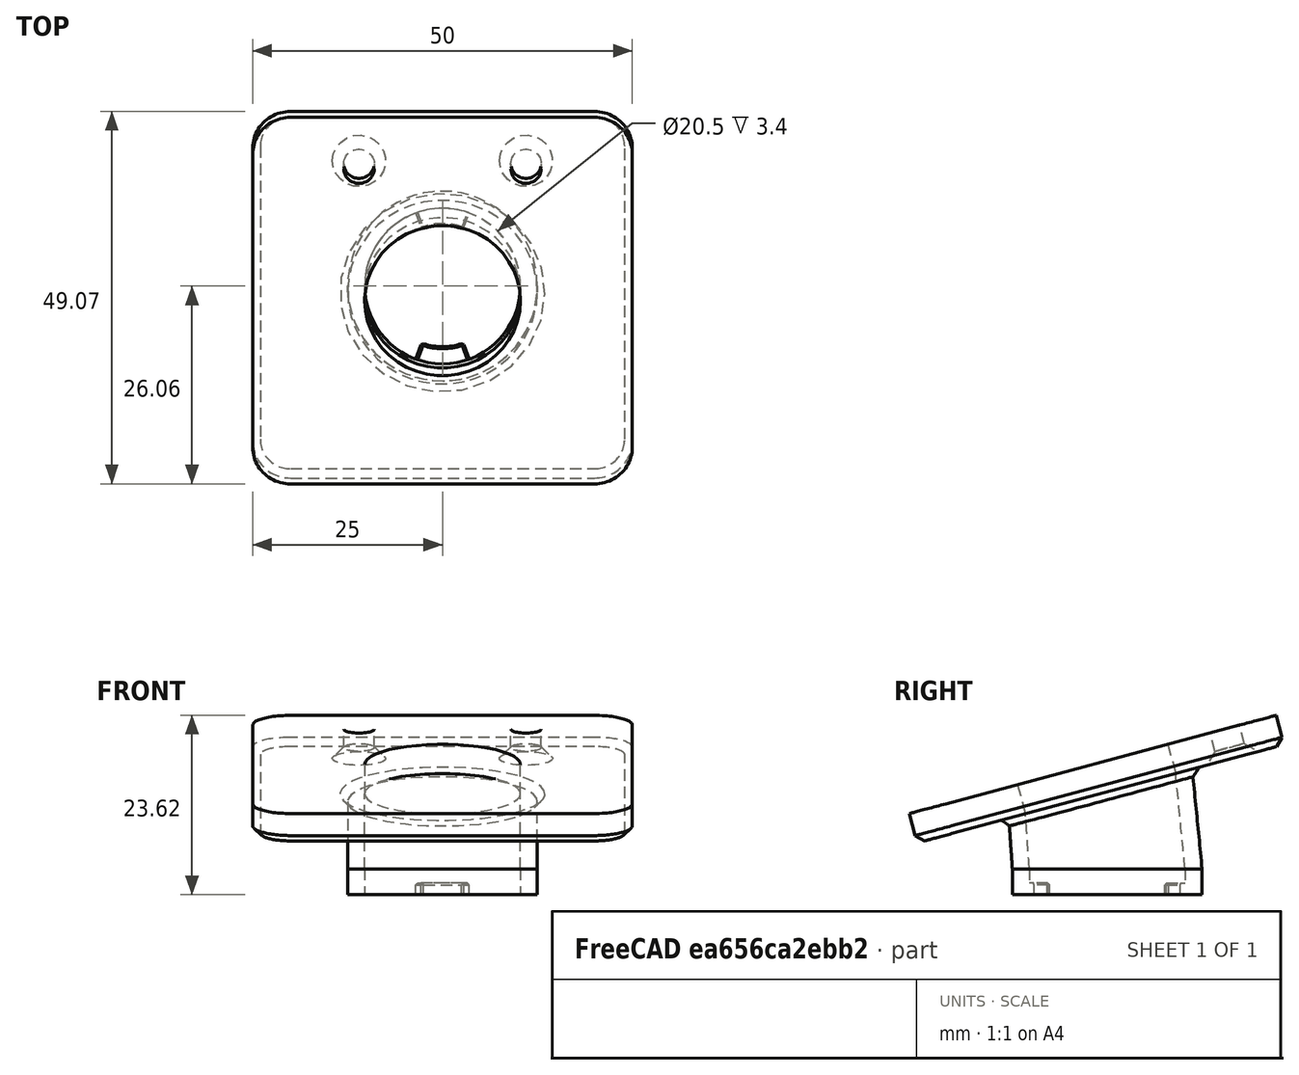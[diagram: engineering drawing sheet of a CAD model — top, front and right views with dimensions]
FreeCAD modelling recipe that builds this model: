
FCSTD DOCUMENT  (FreeCAD 1.1R44874 (Git))
Label: solar_sensor_mount
License: All rights reserved
LicenseURL: https://en.wikipedia.org/wiki/All_rights_reserved
objects: Sketcher::SketchObject×5, PartDesign::Pad×3, PartDesign::PolarPattern×2, PartDesign::Chamfer×2, App::Point×1, PartDesign::SubShapeBinder×1, PartDesign::AdditiveLoft×1, PartDesign::Fillet×1, PartDesign::Hole×1, Part::DatumPlane×1, PartDesign::Body×1
note: 40 computed .brp shape members not serialized (recipe doc carries the construction recipe); baked Part::Feature solids carry a one-line shape summary decoded from their .brp

FEATURE [App::Point] Origin001
  Role = Origin
FEATURE [Sketcher::SketchObject] Sketch
  ArcFitTolerance = 1e-06
  AttachmentSupport = -> [Origin]
  ExternalTypes = [0]
  FullyConstrained = true
  MakeInternals = false
  MapMode = 5
  _ExternalGeoVersion = 1
  sketch-geometry (2):
    g0: Circle CenterX=0 CenterY=0 CenterZ=0 NormalX=0 NormalY=0 NormalZ=1 AngleXU=0 Radius=12.5
    g1: Circle CenterX=0 CenterY=0 CenterZ=0 NormalX=0 NormalY=0 NormalZ=1 AngleXU=0 Radius=10.25
  constraints (4):
    c: Coincident(g1,g0)
    c: Diameter(g0) = 25
    c: Diameter(g1) = 20.5
    c: Coincident(g0,g-1)
FEATURE [PartDesign::Pad] Pad
  Direction = (0,0,1)
  Length = 3.4
  Length2 = 10
  Profile = -> Sketch
  ReferenceAxis = -> Sketch [N_Axis]
  Refine = true
  SideType = 0
  Suppressed = false
  Type = 0
  Type2 = 0
FEATURE [Sketcher::SketchObject] Sketch001
  ArcFitTolerance = 1e-06
  AttachmentSupport = -> [Origin]
  ExternalGeometry = -> [Pad]
  ExternalTypes = [0]
  FullyConstrained = true
  MakeInternals = false
  MapMode = 5
  _ExternalGeoVersion = 1
  sketch-geometry (7):
    g0: ArcOfCircle CenterX=0 CenterY=0 CenterZ=0 NormalX=0 NormalY=0 NormalZ=1 AngleXU=0 Radius=8 StartAngle=1.21989 EndAngle=1.9217
    g1: ArcOfCircle CenterX=0 CenterY=0 CenterZ=0 NormalX=0 NormalY=0 NormalZ=1 AngleXU=0 Radius=10.25 StartAngle=1.21989 EndAngle=1.9217
    g2: LineSegment StartX=-3.52344 StartY=9.62538 StartZ=0 EndX=-2.75 EndY=7.51249 EndZ=0
    g3: LineSegment [constr] StartX=-2.75 StartY=7.51249 StartZ=0 EndX=0 EndY=0 EndZ=0
    g4: LineSegment [constr] StartX=0 StartY=0 StartZ=0 EndX=2.75 EndY=7.51249 EndZ=0
    g5: LineSegment StartX=2.75 StartY=7.51249 StartZ=0 EndX=3.52344 EndY=9.62538 EndZ=0
    g6: LineSegment [constr] StartX=-2.75 StartY=7.51249 StartZ=0 EndX=2.75 EndY=7.51249 EndZ=0
  constraints (19):
    c: Coincident(g0,g-1)
    c: Coincident(g1,g0)
    c: PointOnObject(g1,g-3)
    c: Coincident(g1,g2)
    c: Coincident(g2,g3)
    c: Coincident(g3,g0)
    c: Coincident(g3,g4)
    c: Coincident(g4,g0)
    c: Coincident(g4,g5)
    c: Coincident(g5,g1)
    c: Parallel(g2,g3)
    c: Parallel(g5,g4)
    c: Diameter(g0) = 16
    c: Coincident(g2,g0)
    c: Symmetric(g0,g0,g-2)
    c: PointOnObject(g6,g3)
    c: Coincident(g6,g0)
    c: Horizontal(g6)
    c: DistanceX(g6,g6) = 5.5
FEATURE [PartDesign::Pad] Pad001
  BaseFeature = -> Pad
  Direction = (0,0,1)
  Length = 1.5
  Length2 = 10
  Profile = -> Sketch001
  ReferenceAxis = -> Sketch001 [N_Axis]
  Refine = true
  SideType = 0
  Suppressed = false
  Type = 0
  Type2 = 0
FEATURE [PartDesign::PolarPattern] PolarPattern
  Angle = 360
  Axis = -> Z_Axis
  BaseFeature = -> Pad001
  Mode = 0
  Occurrences = 2
  Offset = 120
  Originals = -> [Pad001]
  Refine = true
  SpacingPattern = [0]
  Spacings = [-1]
  Suppressed = false
  TransformMode = 0
FEATURE [PartDesign::Chamfer] Chamfer
  Angle = 45
  Base = -> PolarPattern [Edge22,Edge20,Edge17,Edge15,Edge18]
  BaseFeature = -> PolarPattern
  ChamferType = 0
  FlipDirection = false
  Refine = true
  Size = 0.25
  Size2 = 1
  SupportTransform = false
  Suppressed = false
  UseAllEdges = false
FEATURE [PartDesign::PolarPattern] PolarPattern001
  Angle = 360
  Axis = -> Z_Axis
  BaseFeature = -> Chamfer
  Mode = 0
  Occurrences = 2
  Offset = 120
  Originals = -> [Chamfer]
  Refine = true
  SpacingPattern = [0]
  Spacings = [-1]
  Suppressed = false
  TransformMode = 0
FEATURE [PartDesign::SubShapeBinder] Binder
  BindCopyOnChange = 0
  BindMode = 0
  ClaimChildren = false
  Context = -> Body [Binder.]
  Fuse = false
  MakeFace = true
  OffsetFill = false
  OffsetIntersection = false
  OffsetJoinType = 0
  OffsetOpenResult = false
  PartialLoad = false
  Placement = pos=(0,0,10) rot=(1,0,0;0.261799rad)
  Refine = true
  Relative = true
  Support = -> [PolarPattern001[Face16]]
  _Version = 2
FEATURE [Sketcher::SketchObject] Sketch002
  ArcFitTolerance = 1e-06
  AttachmentSupport = -> [Binder]
  ExternalGeometry = -> [Binder]
  ExternalTypes = [0]
  FullyConstrained = true
  MakeInternals = false
  MapMode = 5
  Placement = pos=(0,-0.879985,13.2841) rot=(1,0,0;0.261799rad)
  _ExternalGeoVersion = 1
  sketch-geometry (7):
    g0: LineSegment StartX=-25 StartY=-25 StartZ=0 EndX=25 EndY=-25 EndZ=0
    g1: LineSegment StartX=25 StartY=-25 StartZ=0 EndX=25 EndY=25 EndZ=0
    g2: LineSegment StartX=25 StartY=25 StartZ=0 EndX=-25 EndY=25 EndZ=0
    g3: LineSegment StartX=-25 StartY=25 StartZ=0 EndX=-25 EndY=-25 EndZ=0
    g4: GeomPoint [constr] X=0 Y=0 Z=0
    g5: Circle [constr] CenterX=-11 CenterY=20 CenterZ=0 NormalX=0 NormalY=0 NormalZ=1 AngleXU=0 Radius=2
    g6: Circle [constr] CenterX=11 CenterY=20 CenterZ=0 NormalX=0 NormalY=0 NormalZ=1 AngleXU=0 Radius=2
  constraints (17):
    c: Coincident(g0,g1)
    c: Coincident(g1,g2)
    c: Coincident(g2,g3)
    c: Coincident(g3,g0)
    c: Horizontal(g0)
    c: Horizontal(g2)
    c: Vertical(g1)
    c: Vertical(g3)
    c: Symmetric(g2,g0,g4)
    c: Coincident(g4,g-1)
    c: Equal(g2,g1)
    c: Symmetric(g5,g6,g-2)
    c: Equal(g5,g6)
    c: Diameter(g5) = 4
    c: DistanceX(g5,g6) = 22
    c: DistanceY(g4,g5) = 20
    c: DistanceY(g5,g2) = 5
FEATURE [PartDesign::AdditiveLoft] AdditiveLoft
  BaseFeature = -> PolarPattern001
  Closed = false
  Profile = -> PolarPattern001 [Face16]
  Refine = true
  Ruled = false
  Sections = -> [Binder]
  Suppressed = false
FEATURE [PartDesign::Pad] Pad002
  BaseFeature = -> AdditiveLoft
  Direction = (0,-0.258819,0.965926)
  Length = 4
  Length2 = 10
  Profile = -> Sketch002
  ReferenceAxis = -> Sketch002 [N_Axis]
  Refine = true
  SideType = 0
  Suppressed = false
  Type = 0
  Type2 = 0
FEATURE [PartDesign::Fillet] Fillet
  Base = -> Pad002 [Edge78,Edge75,Edge77,Edge76]
  BaseFeature = -> Pad002
  Radius = 5
  Refine = true
  SupportTransform = false
  Suppressed = false
  UseAllEdges = false
FEATURE [PartDesign::Chamfer] Chamfer001
  Angle = 45
  Base = -> Fillet [Face11]
  BaseFeature = -> Fillet
  ChamferType = 0
  FlipDirection = false
  Refine = true
  Size = 1
  Size2 = 1
  SupportTransform = false
  Suppressed = false
  UseAllEdges = false
FEATURE [Sketcher::SketchObject] Sketch003
  ArcFitTolerance = 1e-06
  AttachmentSupport = -> [Binder]
  ExternalTypes = [0]
  FullyConstrained = true
  MakeInternals = false
  MapMode = 5
  Placement = pos=(0,-0.879985,13.2841) rot=(1,0,0;0.261799rad)
  _ExternalGeoVersion = 1
  sketch-geometry (2):
    g0: Circle CenterX=-11 CenterY=18 CenterZ=0 NormalX=0 NormalY=0 NormalZ=1 AngleXU=0 Radius=1.5
    g1: Circle CenterX=11 CenterY=18 CenterZ=0 NormalX=0 NormalY=0 NormalZ=1 AngleXU=0 Radius=1.5
  constraints (5):
    c: Symmetric(g0,g1,g-2)
    c: Equal(g0,g1)
    c: DistanceY(g-1,g0) = 18
    c: DistanceX(g0,g1) = 22
    c: Diameter(g0) = 3
FEATURE [PartDesign::Hole] Hole
  BaseFeature = -> Chamfer001
  BaseProfileType = 7
  CustomThreadClearance = 0
  Depth = 25
  DepthType = 0
  Diameter = 4
  DrillForDepth = false
  DrillPoint = 1
  DrillPointAngle = 118
  HoleCutCountersinkAngle = 90
  HoleCutCustomValues = false
  HoleCutDepth = 3.5
  HoleCutDiameter = 7
  HoleCutType = 2
  ModelThread = false
  Profile = -> Sketch003
  Refine = true
  Reversed = true
  Suppressed = false
  Tapered = false
  TaperedAngle = 90
  ThreadClass = 0
  ThreadDepth = 25
  ThreadDepthType = 0
  ThreadDiameter = 4
  ThreadDirection = 0
  ThreadFit = 0
  ThreadSize = 0
  ThreadType = 0
  Threaded = false
  UseCustomThreadClearance = false
FEATURE [Part::DatumPlane] DatumPlane
  AttachmentSupport = -> [Pad001]
  MapMode = 5
  Placement = pos=(0,0,3.4) rot=(0,0,1;0rad)
FEATURE [Sketcher::SketchObject] Sketch004
  ArcFitTolerance = 1e-06
  AttachmentSupport = -> [DatumPlane]
  ExternalTypes = [0]
  FullyConstrained = true
  MakeInternals = false
  MapMode = 5
  Placement = pos=(0,0,3.4) rot=(0,0,1;0rad)
  _ExternalGeoVersion = 1
  sketch-geometry (13):
    g0: LineSegment StartX=-25 StartY=-35 StartZ=0 EndX=25 EndY=-35 EndZ=0
    g1: LineSegment StartX=35 StartY=-25 StartZ=0 EndX=35 EndY=25 EndZ=0
    g2: LineSegment StartX=25 StartY=35 StartZ=0 EndX=-25 EndY=35 EndZ=0
    g3: LineSegment StartX=-35 StartY=25 StartZ=0 EndX=-35 EndY=-25 EndZ=0
    g4: GeomPoint [constr] X=0 Y=0 Z=0
    g5: ArcOfCircle CenterX=25 CenterY=25 CenterZ=0 NormalX=0 NormalY=0 NormalZ=1 AngleXU=0 Radius=10 StartAngle=0 EndAngle=1.5708
    g6: GeomPoint [constr] X=35 Y=35 Z=0
    g7: ArcOfCircle CenterX=25 CenterY=-25 CenterZ=0 NormalX=0 NormalY=0 NormalZ=1 AngleXU=0 Radius=10 StartAngle=4.71239 EndAngle=6.28319
    g8: GeomPoint [constr] X=35 Y=-35 Z=0
    g9: ArcOfCircle CenterX=-25 CenterY=-25 CenterZ=0 NormalX=0 NormalY=0 NormalZ=1 AngleXU=0 Radius=10 StartAngle=3.14159 EndAngle=4.71239
    g10: GeomPoint [constr] X=-35 Y=-35 Z=0
    g11: ArcOfCircle CenterX=-25 CenterY=25 CenterZ=0 NormalX=0 NormalY=0 NormalZ=1 AngleXU=0 Radius=10 StartAngle=1.5708 EndAngle=3.14159
    g12: GeomPoint [constr] X=-35 Y=35 Z=0
  constraints (28):
    c: Horizontal(g0)
    c: Horizontal(g2)
    c: Vertical(g1)
    c: Vertical(g3)
    c: Symmetric(g6,g10,g4)
    c: Distance(g8,g10) = 70
    c: PointOnObject(g6,g2)
    c: PointOnObject(g6,g1)
    c: Tangent(g2,g5) = -1.5708
    c: Tangent(g1,g5) = -1.5708
    c: PointOnObject(g8,g0)
    c: PointOnObject(g8,g1)
    c: Tangent(g0,g7) = -1.5708
    c: Tangent(g1,g7) = -1.5708
    c: PointOnObject(g10,g0)
    c: PointOnObject(g10,g3)
    c: Tangent(g0,g9) = -1.5708
    c: Tangent(g3,g9) = -1.5708
    c: PointOnObject(g12,g3)
    c: PointOnObject(g12,g2)
    c: Tangent(g3,g11) = -1.5708
    c: Tangent(g2,g11) = -1.5708
    c: Equal(g11,g5)
    c: Equal(g11,g9)
    c: Equal(g11,g7)
    c: Radius(g11) = 10
    c: Equal(g0,g1)
    c: Coincident(g4,g-1)
FEATURE [PartDesign::Body] Body
  AllowCompound = true
  Group = -> [Sketch,Pad,Sketch001,Pad001,PolarPattern,Chamfer,PolarPattern001,Binder,Sketch002,AdditiveLoft,Pad002,Fillet,Chamfer001,Sketch003,Hole,DatumPlane,Sketch004]
  Origin = -> Origin
  Tip = -> Hole
